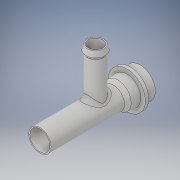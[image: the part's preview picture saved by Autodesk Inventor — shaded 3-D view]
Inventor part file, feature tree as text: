
AUTODESK INVENTOR PART (.ipt)
format: ipt  version: 2019 (Build 230136000, 136)  size: 244,224 bytes
history: native  units: mm
features: sketch x7, extrude x5, fillet x3, revolve x2
ambient origin geometry x8: Origin, YZ Plane, XZ Plane, XY Plane, X Axis, Y Axis, Z Axis, Center Point
bodies: Solid1 (feature_tree)
feature tree (17):
  extrude  "Extrusion1"  Depth=18.0mm
  extrude  "Extrusion2"  Depth=20.0mm
  extrude  "Extrusion3"  Depth=20.0mm TaperAngle=0.0deg
  extrude  "Extrusion4"  Depth=13.0mm
  extrude  "Extrusion5"  Depth=13.0mm
  fillet  "Fillet1"  Radius=20.0mm
  fillet  "Fillet2"  Radius=18.0mm
  revolve  "Revolution1"  [1 undecoded]
  revolve  "Revolution2"  [1 undecoded]
  fillet  "Fillet3"  Radius=16.580628mm
  sketch  "Sketch1"  dims[d0=20.0mm d1=18.0mm]
  sketch  "Sketch2"  dims[d2=50.0mm d3=0.0mm d4=20.0mm]
  sketch  "Sketch3"  dims[d5=18.0mm d6=20.0mm d7=0.0mm]
  sketch  "Sketch4"  dims[d8=15.0mm d9=13.0mm]
  sketch  "Sketch5"  dims[d10=50.0mm d11=0.0mm d12=13.0mm d13=20.0mm d14=0.0mm d15=18.0mm]
  sketch  "Sketch6"  dims[d16=30.0mm d17=0.0mm d18=2.0mm]
  sketch  "Sketch7"  dims[d19=4.0mm d20=20.0mm d24=16.580628mm d25=20.0mm d26=2.0mm d27=4.0mm d28=90.0deg d31=4.0mm d32=90.0deg d33=1.0mm]
note: 2 required parameter values undecoded (feature->parameter linkage not recoverable at this tier; creation-order binding heuristic only, values carry confidence <= 0.55)
